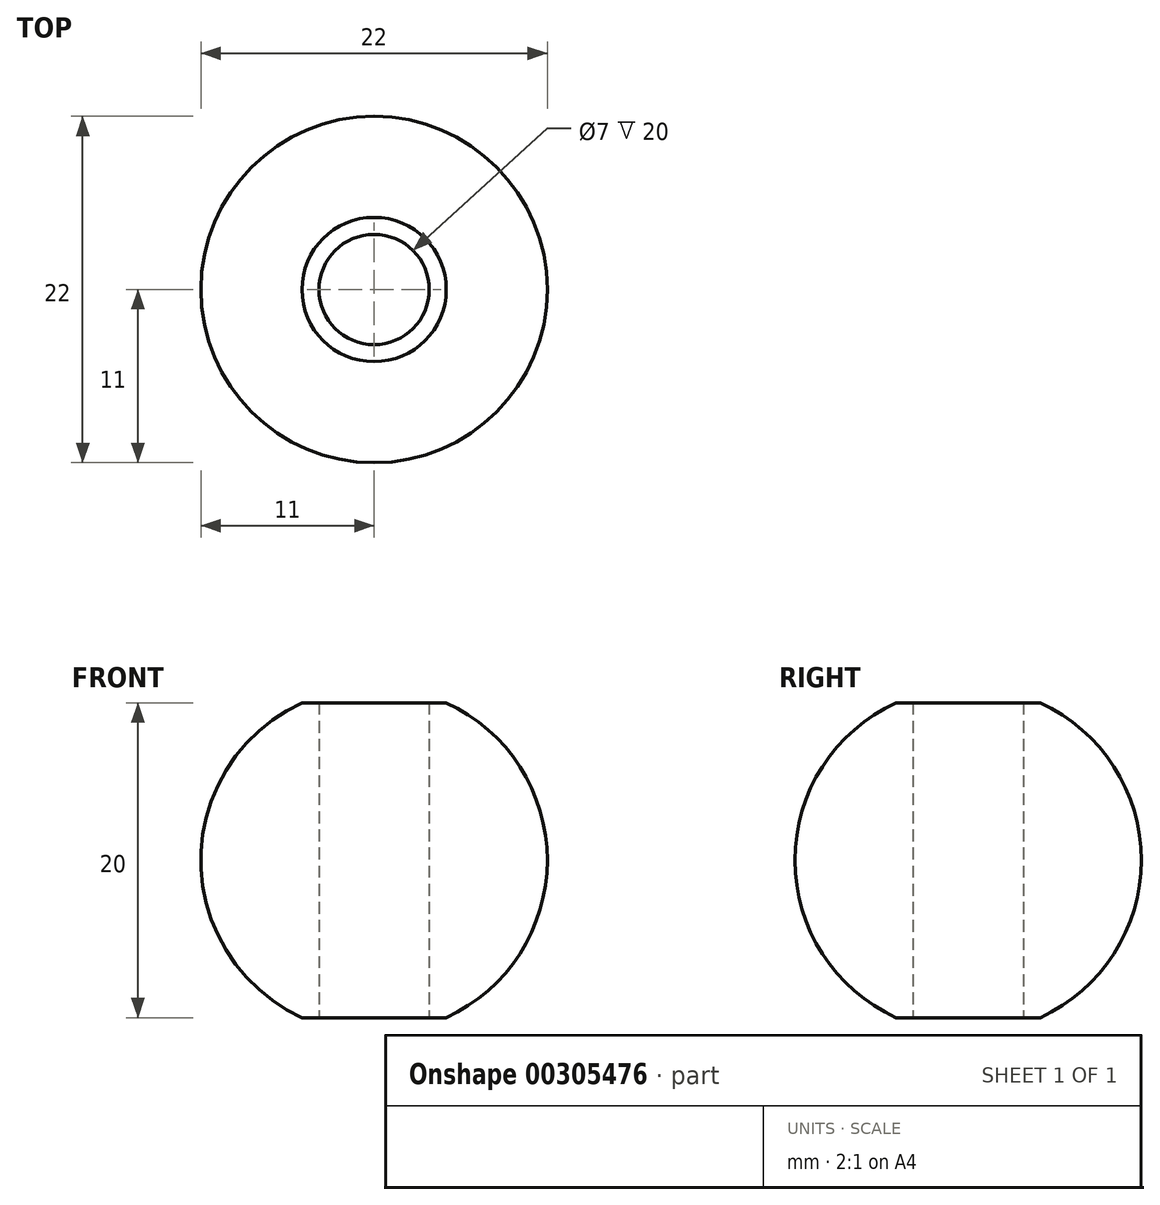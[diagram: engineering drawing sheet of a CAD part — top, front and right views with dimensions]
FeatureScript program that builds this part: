
annotation { "Feature Type Name" : "Feature", "Feature Type Description" : "" }
export const myFeature = defineFeature(function(context is Context, id is Id, definition is map)
    precondition{}
    {
        {
            var Q0;
            Q0=qCreatedBy(makeId("Front.planeOp"),FACE);
            var sketch = newSketch(context, id + "F0", { "sketchPlane" : qUnion([Q0])});
            skCircle(sketch, "E0", {"center": v(0, 0) * mm, "radius": 11 * mm});
            skLineSegment(sketch, "E1", {"start": v(0, -11) * mm, "end": v(0, 11) * mm, "construction": true});
            skLineSegment(sketch, "E2.bottom", {"start": v(20.06, 10) * mm, "end": v(-20.06, 10) * mm});
            skLineSegment(sketch, "E2.top", {"start": v(20.06, -10) * mm, "end": v(-20.06, -10) * mm});
            skLineSegment(sketch, "E2.left", {"start": v(20.06, 10) * mm, "end": v(20.06, -10) * mm});
            skLineSegment(sketch, "E2.right", {"start": v(-20.06, 10) * mm, "end": v(-20.06, -10) * mm});
            skLineSegment(sketch, "E3", {"start": v(3.5, 10) * mm, "end": v(3.5, -10) * mm});
            skSolve(sketch);
        }
        {
            var Q0;
            {var subQ5=sQuery(id+"F0.wireOp",EDGE,"E3");Q0=makeQuery(id+"F0.imprint","IMPRINT",FACE,{"disambiguationData":[TD([[makeQuery(id+"F0.imprint","IMPRINT",EDGE,{"derivedFrom":subQ5}),1.0]])]});}
            var Q1;
            Q1=sQuery(id+"F0.wireOp",EDGE,"E1");
            revolve(context, id + "F1", {"entities" : qUnion([Q0]), "axis" : qUnion([Q1]), "revolveType" : RevolveType.FULL});
        }
    });
